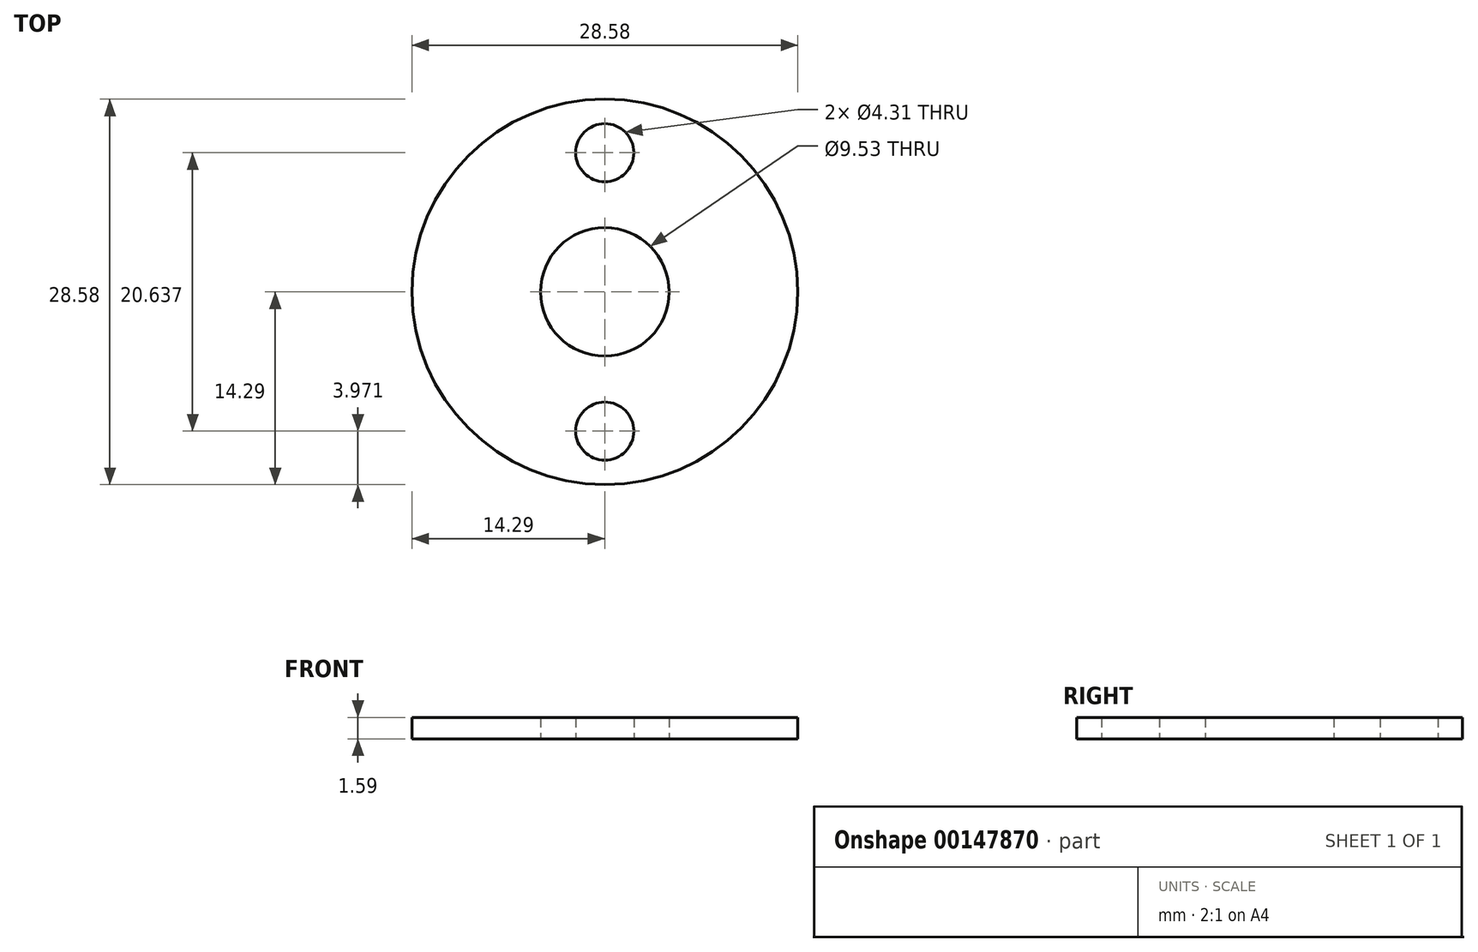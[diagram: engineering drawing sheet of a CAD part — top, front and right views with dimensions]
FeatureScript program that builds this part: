
annotation { "Feature Type Name" : "Feature", "Feature Type Description" : "" }
export const myFeature = defineFeature(function(context is Context, id is Id, definition is map)
    precondition{}
    {
        {
            var Q0;
            Q0=qCreatedBy(makeId("Top.planeOp"),FACE);
            var sketch = newSketch(context, id + "F0", { "sketchPlane" : qUnion([Q0])});
            skCircle(sketch, "E0", {"center": v(0, 0) * mm, "radius": 14.29 * mm});
            skCircle(sketch, "E1", {"center": v(0, -10.32) * mm, "radius": 3.97 * mm, "construction": true});
            skCircle(sketch, "E2", {"center": v(0, -10.32) * mm, "radius": 2.15 * mm});
            skLineSegment(sketch, "E3", {"start": v(0, 10.32) * mm, "end": v(0, -10.32) * mm, "construction": true});
            skCircle(sketch, "E4", {"center": v(0, 10.32) * mm, "radius": 2.15 * mm});
            skCircle(sketch, "E5", {"center": v(0, 0) * mm, "radius": 4.76 * mm});
            skSolve(sketch);
        }
        {
            var Q0;
            Q0=makeQuery(id+"F0.imprint","IMPRINT",FACE,{"disambiguationData":[TD([[makeQuery(id+"F0.imprint","IMPRINT",EDGE,{"derivedFrom":sQuery(id+"F0.wireOp",EDGE,"d7zeTPih-CRss-xDOh-gPdP-rmPCdwzH7cdN.left")}),1.0]])]});
            var Q1;
            Q1=makeQuery(id+"F0.imprint","IMPRINT",FACE,{"disambiguationData":[TD([[makeQuery(id+"F0.imprint","IMPRINT",EDGE,{"derivedFrom":sQuery(id+"F0.wireOp",EDGE,"E0")}),1.0]])]});
            extrude(context, id + "F1", {"entities" : qUnion([Q0, Q1]), "depth" : 1.59 * mm});
        }
    });
